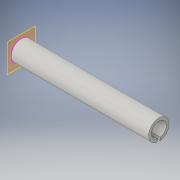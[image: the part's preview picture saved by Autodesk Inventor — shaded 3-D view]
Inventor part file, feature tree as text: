
AUTODESK INVENTOR PART (.ipt)
format: ipt  version: 2016 (Build 200138000, 138)  size: 122,368 bytes
history: native  units: in
note: dims shown in document units (in); Inventor stores cm internally (conversion verified against a paired STEP export)
features: plane x4, sketch x4, extrude x2
ambient origin geometry x8: Origin, YZ Plane, XZ Plane, XY Plane, X Axis, Y Axis, Z Axis, Center Point
bodies: Solid1 (feature_tree)
feature tree (10):
  plane  "Work Plane1"
  plane  "Work Plane2"
  sketch  "Sketch3"  dims[d6=0.0455in d7=0.0455in]
  plane  "Work Plane3"
  sketch  "Sketch4"  dims[d8=4.25in d9=0.0in d10=0.46in]
  plane  "Work Plane4"
  sketch  "Sketch5"  dims[d11=4.25in d12=0.0in]
  extrude  "Extrusion3"  Depth=0.0455in
  extrude  "Extrusion4"  Depth=4.25in
  sketch  "Sketch6"
